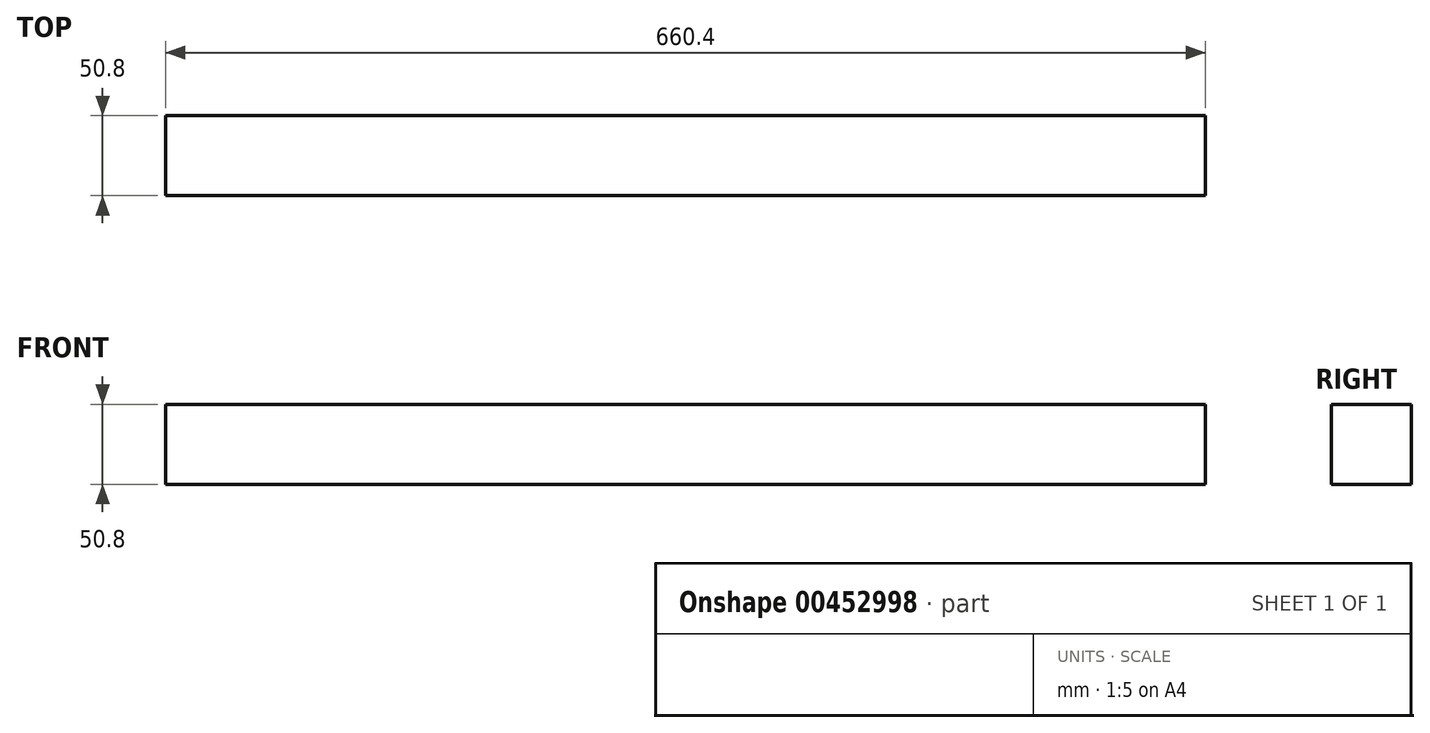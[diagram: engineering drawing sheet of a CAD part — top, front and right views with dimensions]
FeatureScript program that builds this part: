
annotation { "Feature Type Name" : "Feature", "Feature Type Description" : "" }
export const myFeature = defineFeature(function(context is Context, id is Id, definition is map)
    precondition{}
    {
        {
            var Q0;
            Q0=qCreatedBy(makeId("Front.planeOp"),FACE);
            var sketch = newSketch(context, id + "F0", { "sketchPlane" : qUnion([Q0])});
            skLineSegment(sketch, "E0.bottom", {"start": v(330.2, 25.4) * mm, "end": v(-330.2, 25.4) * mm});
            skLineSegment(sketch, "E0.top", {"start": v(330.2, -25.4) * mm, "end": v(-330.2, -25.4) * mm});
            skLineSegment(sketch, "E0.left", {"start": v(330.2, 25.4) * mm, "end": v(330.2, -25.4) * mm});
            skLineSegment(sketch, "E0.right", {"start": v(-330.2, 25.4) * mm, "end": v(-330.2, -25.4) * mm});
            skPoint(sketch, "E0.middle", {"position": v(0, 0) * mm});
            skSolve(sketch);
        }
        {
            var Q0;
            Q0=makeQuery(id+"F0.imprint","IMPRINT",FACE,{"disambiguationData":[TD([[makeQuery(id+"F0.imprint","IMPRINT",EDGE,{"derivedFrom":sQuery(id+"F0.wireOp",EDGE,"E0.bottom")}),1.0]])]});
            extrude(context, id + "F1", {"entities" : qUnion([Q0]), "depth" : 50.8 * mm, "symmetric" : true});
        }
    });
